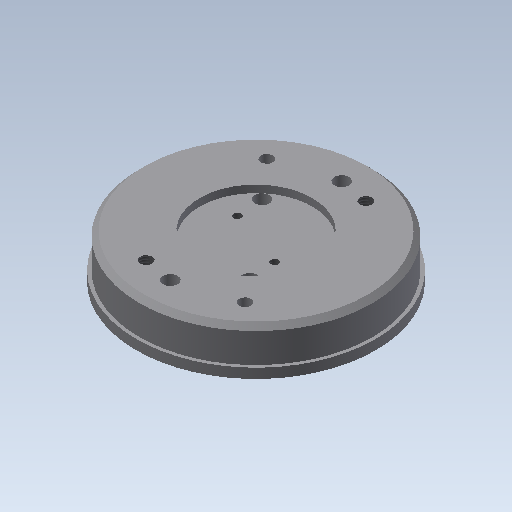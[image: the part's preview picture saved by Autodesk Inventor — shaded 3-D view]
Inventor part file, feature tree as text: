
AUTODESK INVENTOR PART (.ipt)
format: ipt  version: 2020.2 (Build 242310000, 310)  size: 186,880 bytes
history: native  units: mm
features: sketch x6, hole x5, extrude x4, chamfer x2, projected_geometry x2
ambient origin geometry x8: Origin, YZ Plane, XZ Plane, XY Plane, X Axis, Y Axis, Z Axis, Center Point
bodies: Volumenkörper1 (feature_tree)
feature tree (19):
  extrude  "Extrusion1"  Depth=9.0mm TaperAngle=0.0deg
  extrude  "Extrusion2"  Depth=1.5mm TaperAngle=0.0deg
  extrude  "Extrusion3"  Depth=2.0mm
  extrude  "Extrusion4"  Depth=2.0mm
  hole  "Bohrung2"  [1 undecoded]
  hole  "Bohrung3"  [1 undecoded]
  hole  "Bohrung1"  [1 undecoded]
  chamfer  "Fase3"  Distance=47.0mm
  chamfer  "Fase6"  Distance=1.0mm
  hole  "Bohrung9"  [1 undecoded]
  hole  "Bohrung11"  [1 undecoded]
  sketch  "Skizze1"  dims[d0=48.8mm d1=9.0mm d2=0.0mm]
  sketch  "Skizze2"  dims[d5=23.0mm d6=1.5mm d7=0.0mm]
  sketch  "Skizze5"  dims[d9=12.7mm]
  projected_geometry  "Projizierte Kontur1"
  projected_geometry  "Projizierte Kontur2"
  sketch  "Skizze10"  dims[d10=1.567mm d11=20.0mm d12=4.0mm d13=2.0mm d14=90.0deg d15=6.0mm d16=20.594885mm d17=35.0mm]
  sketch  "Skizze12"  dims[d18=3.0mm d19=5.0mm d20=4.0mm d21=2.0mm d22=90.0deg d23=2.0mm d24=20.594885mm d25=3.490659mm]
  sketch  "Skizze17"  dims[d26=3.490659mm d27=2.459mm d28=20.0mm d29=4.0mm d30=2.0mm d31=90.0deg d32=5.0mm d33=20.594885mm d62=47.5mm d63=7.0mm d64=0.0mm d65=1.0mm d66=2.0mm d67=45.0deg d82=47.0mm d83=1.0mm d84=0.0mm d95=1.0mm d96=2.0mm d97=45.0deg d110=20.0mm d111=6.981317mm d115=11.0mm d116=3.0mm d117=6.0mm d118=4.0mm d119=2.0mm d120=90.0deg d121=8.0mm d122=20.594885mm d134=36.0mm d135=2.459mm d136=6.0mm d137=4.0mm d138=2.0mm d139=90.0deg d140=8.0mm d141=20.594885mm d142=20.594885mm d143=0.0625mm d144=0.75mm d145=0.375mm]
note: 5 required parameter values undecoded (feature->parameter linkage not recoverable at this tier; creation-order binding heuristic only, values carry confidence <= 0.55)
